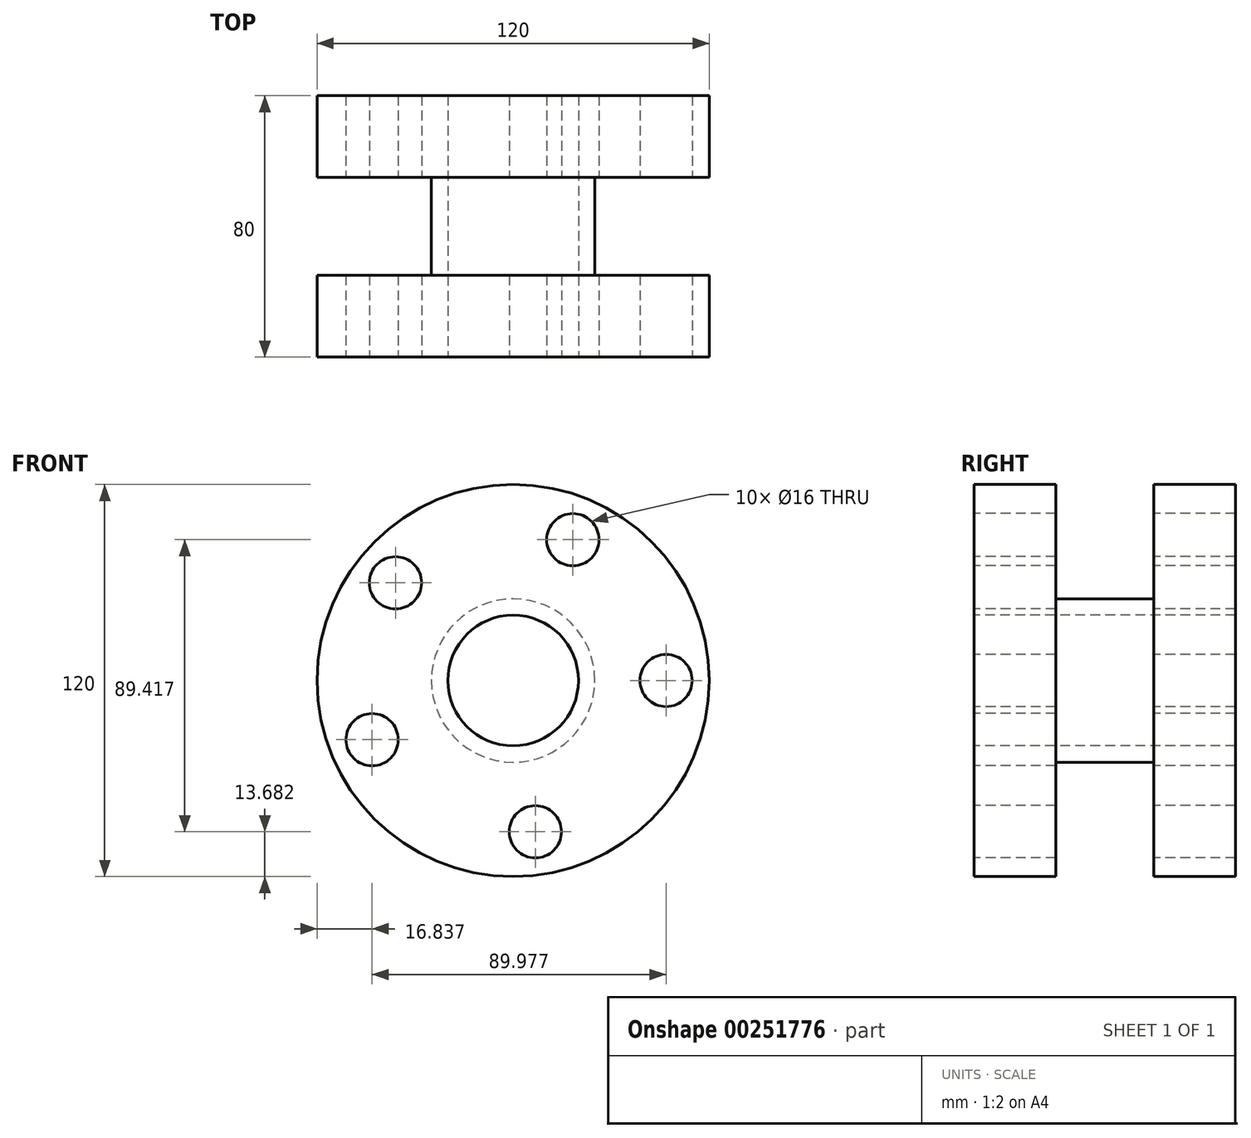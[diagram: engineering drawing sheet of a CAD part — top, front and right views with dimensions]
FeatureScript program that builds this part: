
annotation { "Feature Type Name" : "Feature", "Feature Type Description" : "" }
export const myFeature = defineFeature(function(context is Context, id is Id, definition is map)
    precondition{}
    {
        {
            var Q0;
            Q0=qCreatedBy(makeId("Front.planeOp"),FACE);
            var sketch = newSketch(context, id + "F0", { "sketchPlane" : qUnion([Q0])});
            skCircle(sketch, "E0", {"center": v(0, 0) * mm, "radius": 60 * mm});
            skSolve(sketch);
        }
        {
            var Q0;
            Q0 = qSketchRegion(id + "F0", true);
            extrude(context, id + "F1", {"entities" : qUnion([Q0]), "depth" : 25 * mm});
        }
        {
            var Q0;
            Q0=makeQuery(id+"F1.opExtrude","CAP_FACE",FACE,{"disambiguationData":[OSD([sQuery(id+"F0.wireOp",EDGE,"E0")])],"isStart":true});
            var sketch = newSketch(context, id + "F2", { "sketchPlane" : qUnion([Q0])});
            skCircle(sketch, "E1", {"center": v(0, 0) * mm, "radius": 25 * mm});
            skSolve(sketch);
        }
        {
            var Q0;
            Q0 = qSketchRegion(id + "F2", true);
            extrude(context, id + "F3", {"entities" : qUnion([Q0]), "operationType" : NewBodyOperationType.ADD, "depth" : 30 * mm});
        }
        {
            var Q0;
            Q0=makeQuery(id+"F3.opExtrude","CAP_FACE",FACE,{"disambiguationData":[OSD([sQuery(id+"F2.wireOp",EDGE,"E1")])],"isStart":false});
            var sketch = newSketch(context, id + "F4", { "sketchPlane" : qUnion([Q0])});
            skCircle(sketch, "E2", {"center": v(0, 0) * mm, "radius": 60 * mm});
            skSolve(sketch);
        }
        {
            var Q0;
            Q0 = qSketchRegion(id + "F4", true);
            extrude(context, id + "F5", {"entities" : qUnion([Q0]), "operationType" : NewBodyOperationType.ADD, "depth" : 25 * mm});
        }
        {
            var Q0;
            Q0=makeQuery(id+"F1.opExtrude","CAP_FACE",FACE,{"disambiguationData":[OSD([sQuery(id+"F0.wireOp",EDGE,"E0")])],"isStart":false});
            var sketch = newSketch(context, id + "F6", { "sketchPlane" : qUnion([Q0])});
            skCircle(sketch, "E3", {"center": v(0, 0) * mm, "radius": 20 * mm});
            skSolve(sketch);
        }
        {
            var Q0;
            Q0 = qSketchRegion(id + "F6", true);
            extrude(context, id + "F7", {"entities" : qUnion([Q0]), "operationType" : NewBodyOperationType.REMOVE, "endBound" : BoundingType.THROUGH_ALL, "oppositeDirection" : true, "depth" : 25 * mm});
        }
        {
            var Q0;
            Q0=makeQuery(id+"F1.opExtrude","CAP_FACE",FACE,{"disambiguationData":[OSD([sQuery(id+"F0.wireOp",EDGE,"E0")])],"isStart":false});
            var sketch = newSketch(context, id + "F8", { "sketchPlane" : qUnion([Q0])});
            skCircle(sketch, "E4", {"center": v(-36.02, 29.9) * mm, "radius": 8 * mm});
            skCircle(sketch, "E5", {"center": v(18.28, 43.1) * mm, "radius": 8 * mm});
            skCircle(sketch, "E6", {"center": v(-43.16, -18.13) * mm, "radius": 8 * mm});
            skCircle(sketch, "E7", {"center": v(46.81, 0) * mm, "radius": 8 * mm});
            skCircle(sketch, "E8", {"center": v(6.8, -46.32) * mm, "radius": 8 * mm});
            skSolve(sketch);
        }
        {
            var Q0;
            Q0 = qSketchRegion(id + "F8", true);
            extrude(context, id + "F9", {"entities" : qUnion([Q0]), "operationType" : NewBodyOperationType.REMOVE, "endBound" : BoundingType.THROUGH_ALL, "oppositeDirection" : true, "depth" : 25 * mm});
        }
    });
